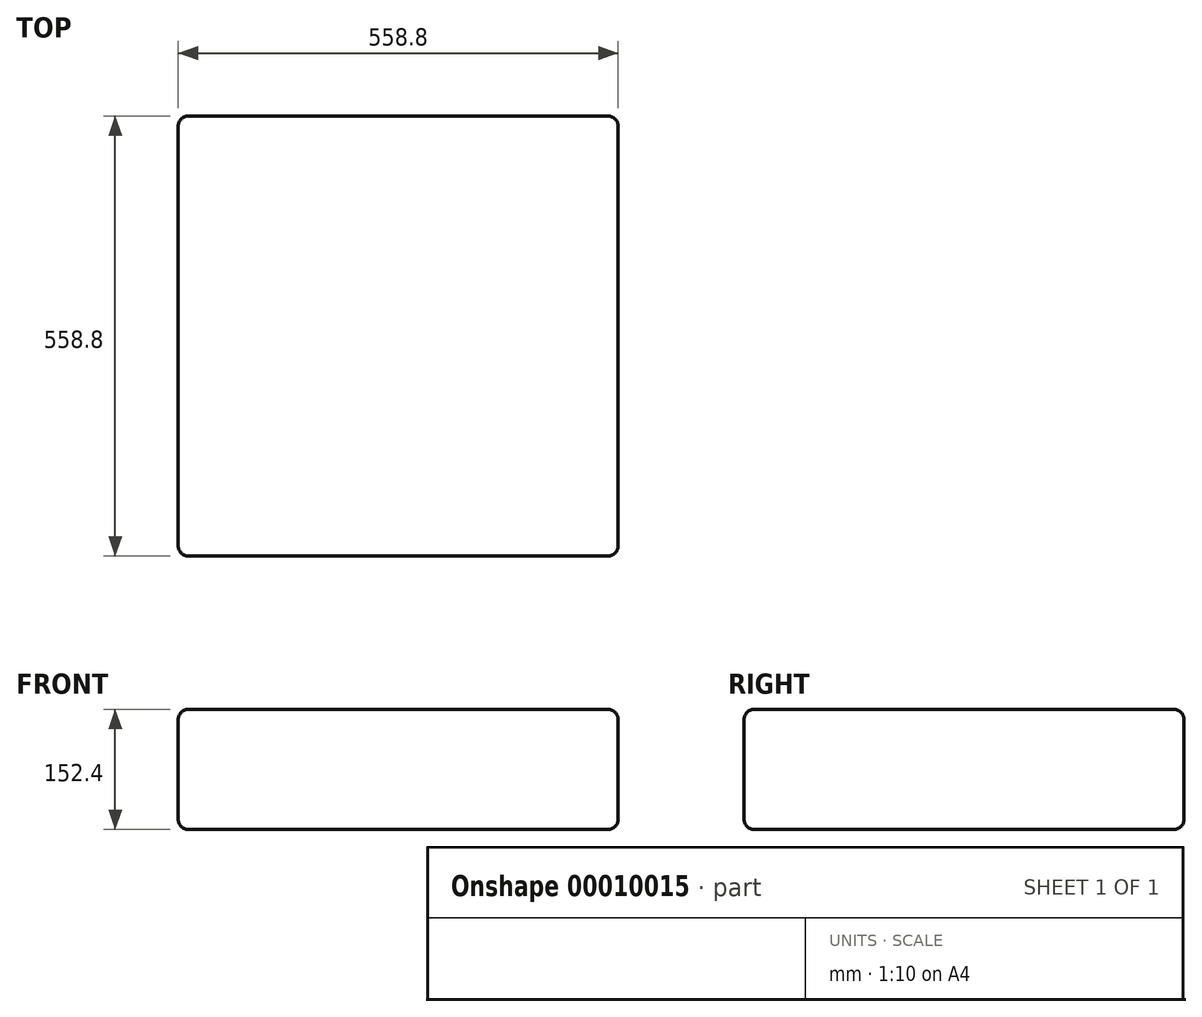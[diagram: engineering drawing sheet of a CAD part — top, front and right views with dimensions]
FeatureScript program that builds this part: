
annotation { "Feature Type Name" : "Feature", "Feature Type Description" : "" }
export const myFeature = defineFeature(function(context is Context, id is Id, definition is map)
    precondition{}
    {
        {
            var Q0;
            Q0=qCreatedBy(makeId("Top.planeOp"),FACE);
            var sketch = newSketch(context, id + "F0", { "sketchPlane" : qUnion([Q0])});
            skLineSegment(sketch, "E0.bottom", {"start": v(-279.4, 279.4) * mm, "end": v(279.4, 279.4) * mm});
            skLineSegment(sketch, "E0.top", {"start": v(-279.4, -279.4) * mm, "end": v(279.4, -279.4) * mm});
            skLineSegment(sketch, "E0.left", {"start": v(-279.4, 279.4) * mm, "end": v(-279.4, -279.4) * mm});
            skLineSegment(sketch, "E0.right", {"start": v(279.4, 279.4) * mm, "end": v(279.4, -279.4) * mm});
            skPoint(sketch, "E0.middle", {"position": v(0, 0) * mm});
            skSolve(sketch);
        }
        {
            var Q0;
            Q0 = qSketchRegion(id + "F0", true);
            extrude(context, id + "F1", {"entities" : qUnion([Q0]), "depth" : 152.4 * mm});
        }
        {
            var Q0;
            Q0=makeQuery(id+"F1.opExtrude","SWEPT_FACE",FACE,{"disambiguationData":[OSD([sQuery(id+"F0.wireOp",EDGE,"E0.top")])]});
            var Q1;
            Q1=makeQuery(id+"F1.opExtrude","SWEPT_EDGE",EDGE,{"disambiguationData":[OSD([sQuery(id+"F0.wireOp",EDGE,"E0.top"),sQuery(id+"F0.wireOp",EDGE,"E0.right")])]});
            var Q2;
            Q2=makeQuery(id+"F1.opExtrude","CAP_FACE",FACE,{"disambiguationData":[OSD([sQuery(id+"F0.wireOp",EDGE,"E0.bottom"),sQuery(id+"F0.wireOp",EDGE,"E0.top"),sQuery(id+"F0.wireOp",EDGE,"E0.left"),sQuery(id+"F0.wireOp",EDGE,"E0.right")])],"isStart":false});
            var Q3;
            Q3=makeQuery(id+"F1.opExtrude","SWEPT_EDGE",EDGE,{"disambiguationData":[OSD([sQuery(id+"F0.wireOp",EDGE,"E0.top"),sQuery(id+"F0.wireOp",EDGE,"E0.left")])]});
            var Q4;
            Q4=makeQuery(id+"F1.opExtrude","CAP_FACE",FACE,{"disambiguationData":[OSD([sQuery(id+"F0.wireOp",EDGE,"E0.bottom"),sQuery(id+"F0.wireOp",EDGE,"E0.top"),sQuery(id+"F0.wireOp",EDGE,"E0.left"),sQuery(id+"F0.wireOp",EDGE,"E0.right")])],"isStart":true});
            var Q5;
            Q5=makeQuery(id+"F1.opExtrude","SWEPT_EDGE",EDGE,{"disambiguationData":[OSD([sQuery(id+"F0.wireOp",EDGE,"E0.bottom"),sQuery(id+"F0.wireOp",EDGE,"E0.right")])]});
            var Q6;
            Q6=makeQuery(id+"F1.opExtrude","SWEPT_FACE",FACE,{"disambiguationData":[OSD([sQuery(id+"F0.wireOp",EDGE,"E0.bottom")])]});
            var Q7;
            Q7=makeQuery(id+"F1.opExtrude","SWEPT_FACE",FACE,{"disambiguationData":[OSD([sQuery(id+"F0.wireOp",EDGE,"E0.left")])]});
            var Q8;
            Q8=makeQuery(id+"F1.opExtrude","CAP_EDGE",EDGE,{"disambiguationData":[OSD([sQuery(id+"F0.wireOp",EDGE,"E0.bottom")])],"isStart":false});
            var Q9;
            Q9=makeQuery(id+"F1.opExtrude","SWEPT_FACE",FACE,{"disambiguationData":[OSD([sQuery(id+"F0.wireOp",EDGE,"E0.right")])]});
            var Q10;
            Q10=makeQuery(id+"F1.opExtrude","CAP_EDGE",EDGE,{"disambiguationData":[OSD([sQuery(id+"F0.wireOp",EDGE,"E0.top")])],"isStart":false});
            var Q11;
            Q11=makeQuery(id+"F1.opExtrude","CAP_EDGE",EDGE,{"disambiguationData":[OSD([sQuery(id+"F0.wireOp",EDGE,"E0.left")])],"isStart":false});
            var Q12;
            Q12=makeQuery(id+"F1.opExtrude","CAP_EDGE",EDGE,{"disambiguationData":[OSD([sQuery(id+"F0.wireOp",EDGE,"E0.right")])],"isStart":true});
            var Q13;
            Q13=makeQuery(id+"F1.opExtrude","CAP_EDGE",EDGE,{"disambiguationData":[OSD([sQuery(id+"F0.wireOp",EDGE,"E0.right")])],"isStart":false});
            var Q14;
            Q14=makeQuery(id+"F1.opExtrude","SWEPT_EDGE",EDGE,{"disambiguationData":[OSD([sQuery(id+"F0.wireOp",EDGE,"E0.bottom"),sQuery(id+"F0.wireOp",EDGE,"E0.left")])]});
            var Q15;
            Q15=makeQuery(id+"F1.opExtrude","CAP_EDGE",EDGE,{"disambiguationData":[OSD([sQuery(id+"F0.wireOp",EDGE,"E0.bottom")])],"isStart":true});
            var Q16;
            Q16=makeQuery(id+"F1.opExtrude","CAP_EDGE",EDGE,{"disambiguationData":[OSD([sQuery(id+"F0.wireOp",EDGE,"E0.top")])],"isStart":true});
            var Q17;
            Q17=makeQuery(id+"F1.opExtrude","CAP_EDGE",EDGE,{"disambiguationData":[OSD([sQuery(id+"F0.wireOp",EDGE,"E0.left")])],"isStart":true});
            fillet(context, id + "F2", {"entities" : qUnion([Q0, Q1, Q2, Q3, Q4, Q5, Q6, Q7, Q8, Q9, Q10, Q11, Q12, Q13, Q14, Q15, Q16, Q17]), "radius" : 12.7 * mm, "tangentPropagation" : true, "allowEdgeOverflow" : false});
        }
    });
